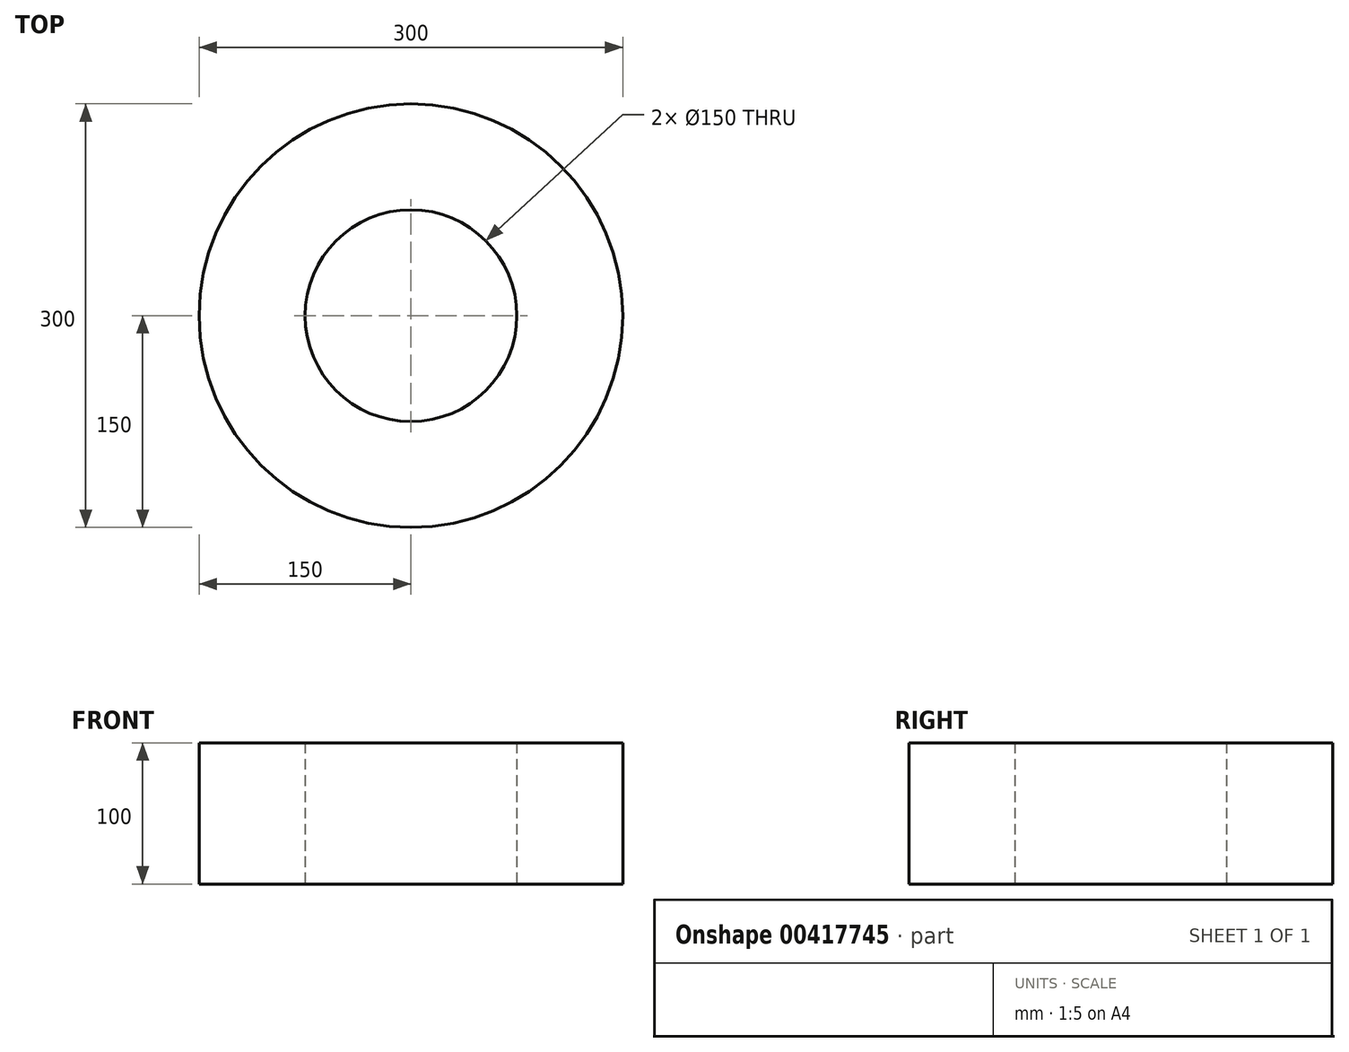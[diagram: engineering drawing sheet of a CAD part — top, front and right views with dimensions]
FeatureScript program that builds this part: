
annotation { "Feature Type Name" : "Feature", "Feature Type Description" : "" }
export const myFeature = defineFeature(function(context is Context, id is Id, definition is map)
    precondition{}
    {
        {
            var Q0;
            Q0=qCreatedBy(makeId("Top.planeOp"),FACE);
            var sketch = newSketch(context, id + "F0", { "sketchPlane" : qUnion([Q0])});
            skCircle(sketch, "E0", {"center": v(0, -4.46) * mm, "radius": 27.92 * mm});
            skSolve(sketch);
        }
        {
            var Q0;
            Q0=makeQuery(id+"F0.imprint","IMPRINT",FACE,{"disambiguationData":[TD([[makeQuery(id+"F0.imprint","IMPRINT",EDGE,{"derivedFrom":sQuery(id+"F0.wireOp",EDGE,"E0")}),1.0]])]});
            extrude(context, id + "F1", {"entities" : qUnion([Q0]), "depth" : 55.37 * mm});
        }
        {
            var Q0;
            Q0=makeQuery(id+"F1.opExtrude","SWEPT_BODY",BODY,{"disambiguationData":[OSD([sQuery(id+"F0.wireOp",EDGE,"E0")])]});
            deleteBodies(context, id + "F2", {"entities" : qUnion([Q0])});
        }
        {
            var Q0;
            Q0=qCreatedBy(makeId("Top.planeOp"),FACE);
            var sketch = newSketch(context, id + "F3", { "sketchPlane" : qUnion([Q0])});
            skCircle(sketch, "E1", {"center": v(0, 0) * mm, "radius": 150 * mm});
            skCircle(sketch, "E2", {"center": v(0, 0) * mm, "radius": 75 * mm});
            skSolve(sketch);
        }
        {
            var Q0;
            Q0=makeQuery(id+"F3.imprint","IMPRINT",FACE,{"disambiguationData":[TD([[makeQuery(id+"F3.imprint","IMPRINT",EDGE,{"derivedFrom":sQuery(id+"F3.wireOp",EDGE,"E1")}),1.0]])]});
            extrude(context, id + "F4", {"entities" : qUnion([Q0]), "depth" : 100 * mm});
        }
    });
